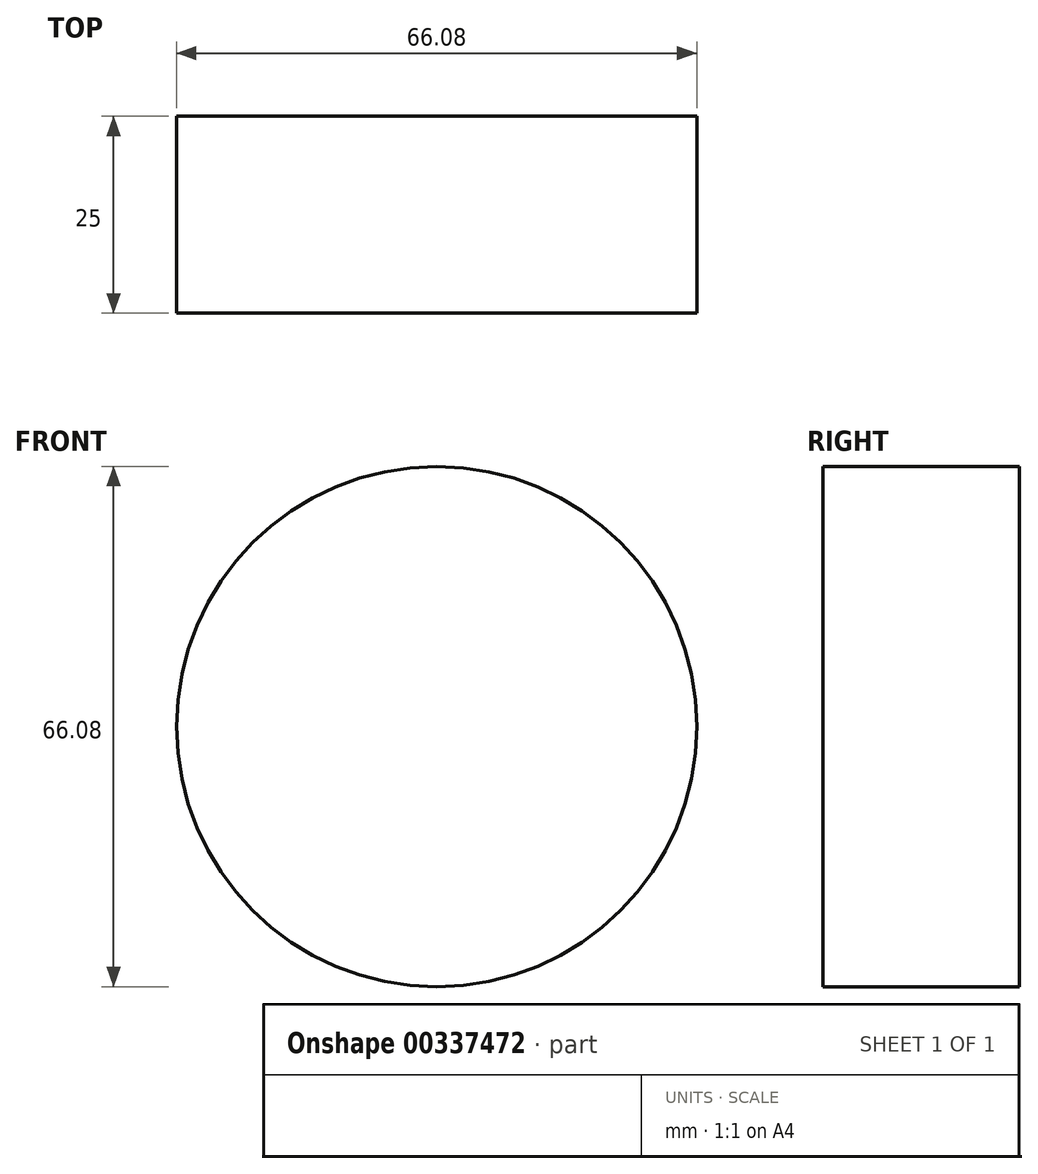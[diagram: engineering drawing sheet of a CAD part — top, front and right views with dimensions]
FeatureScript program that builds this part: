
annotation { "Feature Type Name" : "Feature", "Feature Type Description" : "" }
export const myFeature = defineFeature(function(context is Context, id is Id, definition is map)
    precondition{}
    {
        {
            var Q0;
            Q0=qCreatedBy(makeId("Front.planeOp"),FACE);
            var sketch = newSketch(context, id + "F0", { "sketchPlane" : qUnion([Q0])});
            skCircle(sketch, "E0", {"center": v(0, 0) * mm, "radius": 33.04 * mm});
            skLineSegment(sketch, "E1", {"start": v(0, 0) * mm, "end": v(0, 33.04) * mm});
            skLineSegment(sketch, "E2", {"start": v(0, 0) * mm, "end": v(23.36, 23.36) * mm});
            skLineSegment(sketch, "E3", {"start": v(0, 0) * mm, "end": v(33.04, 0) * mm});
            skSolve(sketch);
        }
        {
            var Q0;
            {var subQ0=sQuery(id+"F0.wireOp",EDGE,"E1");Q0=makeQuery(id+"F0.imprint","IMPRINT",FACE,{"disambiguationData":[TD([[makeQuery(id+"F0.imprint","IMPRINT",EDGE,{"derivedFrom":subQ0}),1.0]])]});}
            var Q1;
            {var subQ0=sQuery(id+"F0.wireOp",EDGE,"E2");Q1=makeQuery(id+"F0.imprint","IMPRINT",FACE,{"disambiguationData":[TD([[makeQuery(id+"F0.imprint","IMPRINT",EDGE,{"derivedFrom":subQ0}),-1.0]])]});}
            var Q2;
            {var subQ0=sQuery(id+"F0.wireOp",EDGE,"E1");Q2=makeQuery(id+"F0.imprint","IMPRINT",FACE,{"disambiguationData":[TD([[makeQuery(id+"F0.imprint","IMPRINT",EDGE,{"derivedFrom":subQ0}),-1.0]])]});}
            extrude(context, id + "F1", {"entities" : qUnion([Q0, Q1, Q2]), "endBound" : BoundingType.SYMMETRIC, "depth" : 25 * mm});
        }
    });
